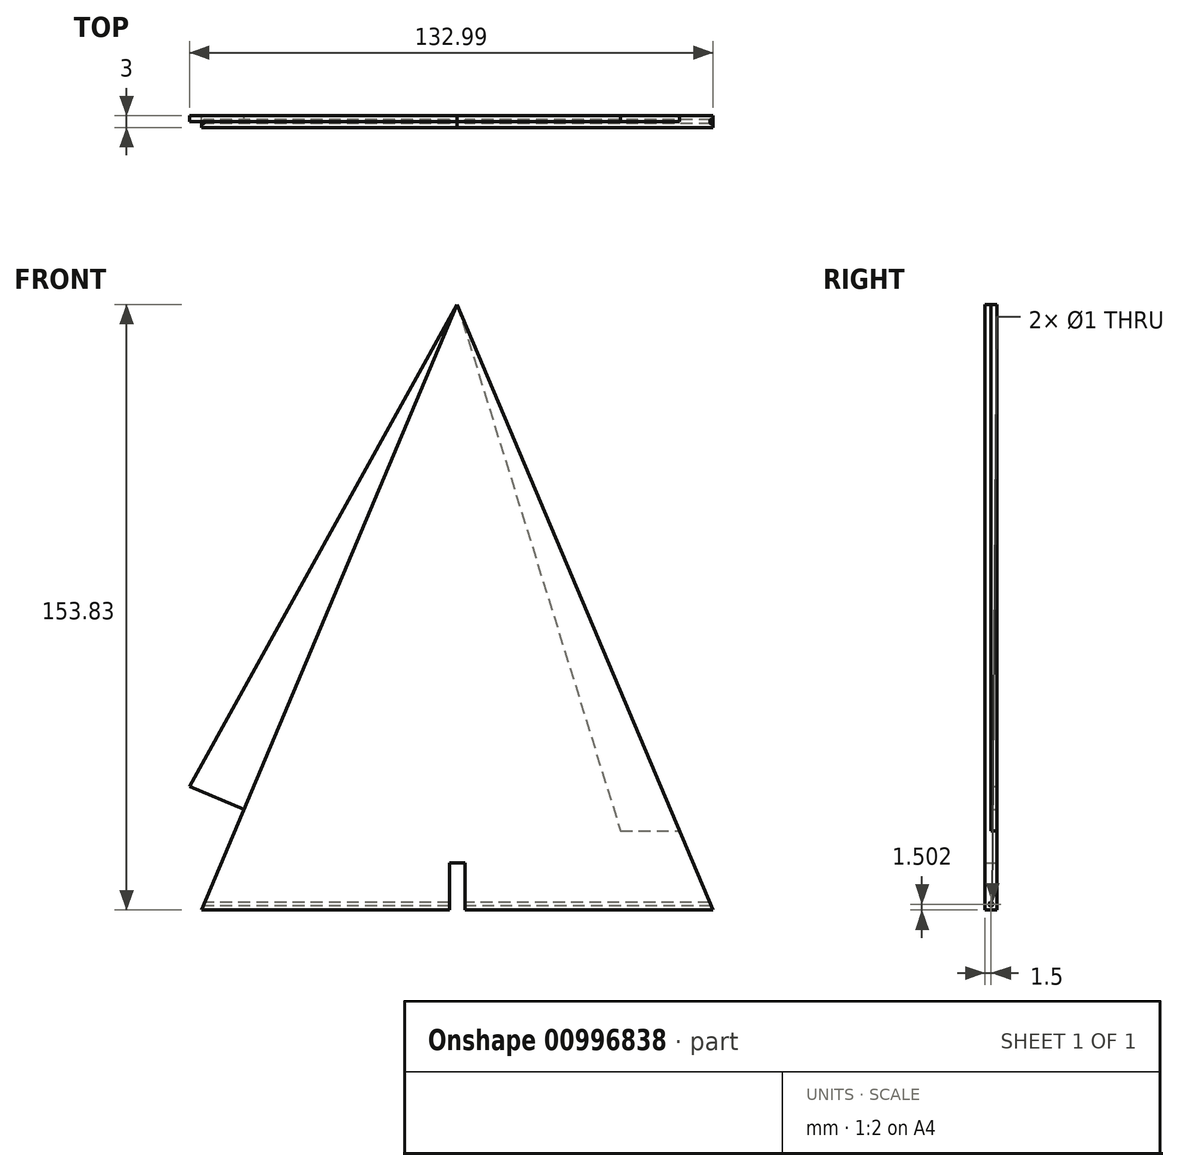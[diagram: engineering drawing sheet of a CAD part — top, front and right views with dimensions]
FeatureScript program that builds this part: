
annotation { "Feature Type Name" : "Feature", "Feature Type Description" : "" }
export const myFeature = defineFeature(function(context is Context, id is Id, definition is map)
    precondition{}
    {
        {
            var Q0;
            Q0=qCreatedBy(makeId("Front.planeOp"),FACE);
            var sketch = newSketch(context, id + "F0", { "sketchPlane" : qUnion([Q0])});
            skLineSegment(sketch, "E0", {"start": v(-65, 113.44) * mm, "end": v(-2, 113.44) * mm});
            skLineSegment(sketch, "E1", {"start": v(-65, 113.44) * mm, "end": v(0, 267.27) * mm});
            skLineSegment(sketch, "E2", {"start": v(0, 267.27) * mm, "end": v(65, 113.44) * mm});
            skLineSegment(sketch, "E3", {"start": v(-2, 113.44) * mm, "end": v(-2, 125.44) * mm});
            skLineSegment(sketch, "E4", {"start": v(-2, 125.44) * mm, "end": v(2, 125.44) * mm});
            skLineSegment(sketch, "E5", {"start": v(2, 125.44) * mm, "end": v(2, 113.44) * mm});
            skLineSegment(sketch, "E6.trimOffspring", {"start": v(2, 113.44) * mm, "end": v(65, 113.44) * mm});
            skLineSegment(sketch, "E7", {"start": v(0, 267.27) * mm, "end": v(41.5, 133.56) * mm});
            skLineSegment(sketch, "E8", {"start": v(41.5, 133.56) * mm, "end": v(56.5, 133.56) * mm});
            skLineSegment(sketch, "E9", {"start": v(0, 267.27) * mm, "end": v(-68, 144.9) * mm});
            skLineSegment(sketch, "E10", {"start": v(-68, 144.9) * mm, "end": v(-54.18, 139.06) * mm});
            skSolve(sketch);
        }
        {
            var Q0;
            Q0 = qSketchRegion(id + "F0", true);
            extrude(context, id + "F1", {"entities" : qUnion([Q0]), "depth" : 3 * mm, "offsetDistance" : 25 * mm});
        }
        {
            var Q0;
            Q0=makeQuery(id+"F1.opExtrude","SWEPT_FACE",FACE,{"disambiguationData":[OSD([sQuery(id+"F0.wireOp",EDGE,"E3")])]});
            var sketch = newSketch(context, id + "F2", { "sketchPlane" : qUnion([Q0])});
            skCircle(sketch, "E11", {"center": v(-1.5, 114.94) * mm, "radius": 0.5 * mm});
            skLineSegment(sketch, "E12", {"start": v(-2, 114.94) * mm, "end": v(-3, 114.94) * mm});
            skLineSegment(sketch, "E13", {"start": v(-1, 114.94) * mm, "end": v(0, 114.94) * mm});
            skLineSegment(sketch, "E14", {"start": v(-1.5, 114.44) * mm, "end": v(-1.5, 113.44) * mm});
            skSolve(sketch);
        }
        {
            var Q0;
            Q0 = qSketchRegion(id + "F2", true);
            extrude(context, id + "F3", {"entities" : qUnion([Q0]), "operationType" : NewBodyOperationType.REMOVE, "depth" : 70 * mm, "offsetDistance" : 25 * mm, "hasSecondDirection" : true, "secondDirectionOppositeDirection" : true, "secondDirectionDepth" : 70 * mm});
        }
        {
            var Q0;
            {var subQ0=sQuery(id+"F0.wireOp",EDGE,"E7");Q0=makeQuery(id+"F0.imprint","IMPRINT",FACE,{"disambiguationData":[TD([[makeQuery(id+"F0.imprint","IMPRINT",EDGE,{"derivedFrom":subQ0}),1.0]])]});}
            extrude(context, id + "F4", {"entities" : qUnion([Q0]), "operationType" : NewBodyOperationType.REMOVE, "depth" : 1.5 * mm, "offsetDistance" : 25 * mm});
        }
        {
            var Q0;
            Q0=makeQuery(id+"F1.opExtrude","CAP_FACE",FACE,{"disambiguationData":[OSD([sQuery(id+"F0.wireOp",EDGE,"E0"),sQuery(id+"F0.wireOp",EDGE,"E1"),sQuery(id+"F0.wireOp",EDGE,"E2"),sQuery(id+"F0.wireOp",EDGE,"E3"),sQuery(id+"F0.wireOp",EDGE,"E4"),sQuery(id+"F0.wireOp",EDGE,"E5"),sQuery(id+"F0.wireOp",EDGE,"E6.trimOffspring"),sQuery(id+"F0.wireOp",EDGE,"E9"),sQuery(id+"F0.wireOp",EDGE,"E10")])],"isStart":false});
            var sketch = newSketch(context, id + "F5", { "sketchPlane" : qUnion([Q0])});
            skLineSegment(sketch, "E15", {"start": v(-54.18, 139.06) * mm, "end": v(-68, 144.9) * mm});
            skLineSegment(sketch, "E16", {"start": v(-68, 144.9) * mm, "end": v(0, 267.27) * mm});
            skLineSegment(sketch, "E17", {"start": v(0, 267.27) * mm, "end": v(-54.18, 139.06) * mm});
            skSolve(sketch);
        }
        {
            var Q0;
            Q0 = qSketchRegion(id + "F5", true);
            extrude(context, id + "F6", {"entities" : qUnion([Q0]), "operationType" : NewBodyOperationType.REMOVE, "oppositeDirection" : true, "depth" : 1.5 * mm, "offsetDistance" : 25 * mm});
        }
    });
